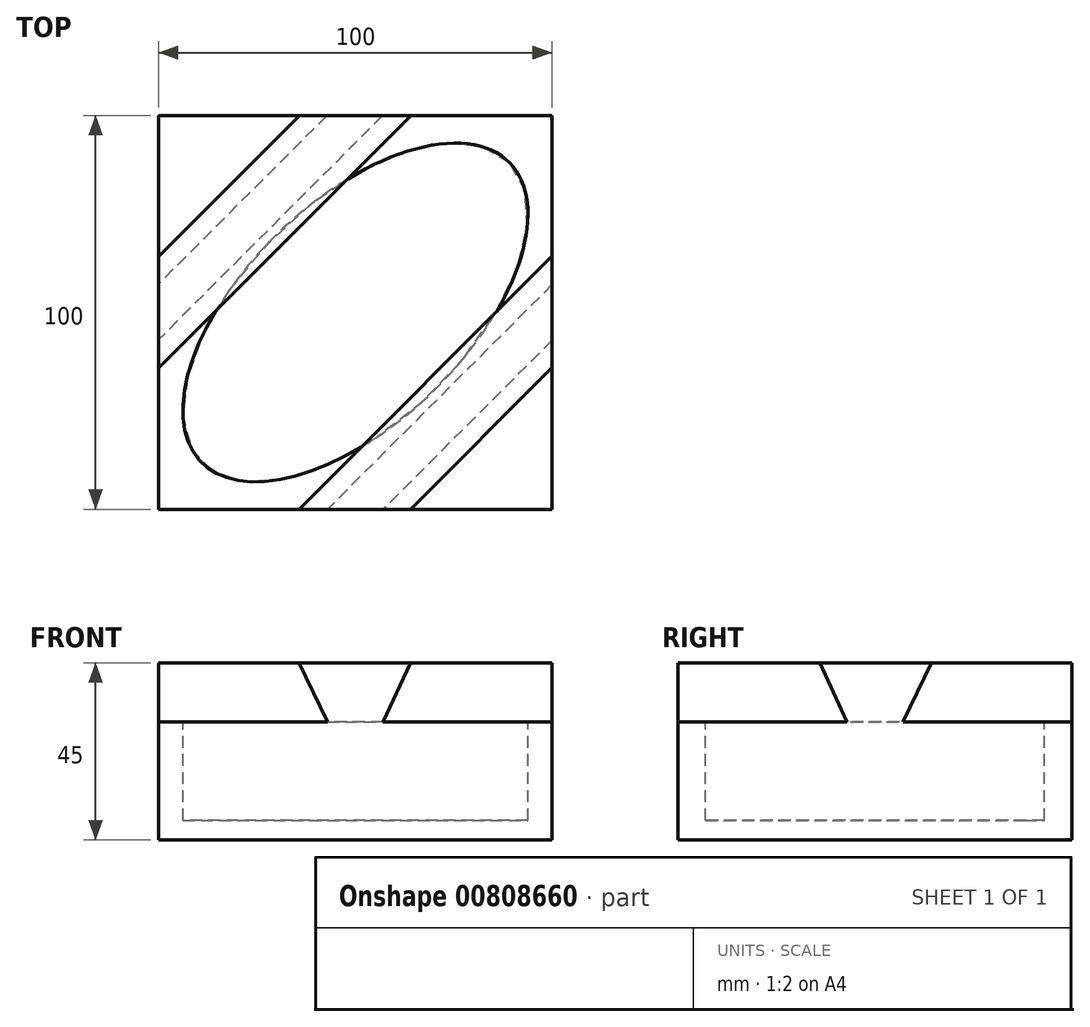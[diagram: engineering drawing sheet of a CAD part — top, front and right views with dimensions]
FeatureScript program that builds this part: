
annotation { "Feature Type Name" : "Feature", "Feature Type Description" : "" }
export const myFeature = defineFeature(function(context is Context, id is Id, definition is map)
    precondition{}
    {
        {
            var Q0;
            Q0=qCreatedBy(makeId("Top.planeOp"),FACE);
            var sketch = newSketch(context, id + "F0", { "sketchPlane" : qUnion([Q0])});
            skLineSegment(sketch, "E0.bottom", {"start": v(-50, 50) * mm, "end": v(50, 50) * mm});
            skLineSegment(sketch, "E0.top", {"start": v(-50, -50) * mm, "end": v(50, -50) * mm});
            skLineSegment(sketch, "E0.left", {"start": v(-50, 50) * mm, "end": v(-50, -50) * mm});
            skLineSegment(sketch, "E0.right", {"start": v(50, 50) * mm, "end": v(50, -50) * mm});
            skPoint(sketch, "E0.middle", {"position": v(0, 0) * mm});
            skLineSegment(sketch, "E1", {"start": v(50, -7.07) * mm, "end": v(7.07, -50) * mm});
            skLineSegment(sketch, "E2", {"start": v(46.46, 3.54) * mm, "end": v(50, 7.07) * mm});
            skLineSegment(sketch, "E3", {"start": v(46.46, 3.54) * mm, "end": v(-7.07, -50) * mm});
            skLineSegment(sketch, "E4", {"start": v(-50.16, 7.07) * mm, "end": v(-7.23, 50) * mm});
            skLineSegment(sketch, "E5", {"start": v(-46.62, -3.54) * mm, "end": v(-50.16, -7.07) * mm});
            skLineSegment(sketch, "E6", {"start": v(-46.62, -3.54) * mm, "end": v(6.91, 50) * mm});
            skSolve(sketch);
        }
        {
            var Q0;
            {var subQ0=sQuery(id+"F0.wireOp",EDGE,"E0.left");var subQ1=sQuery(id+"F0.wireOp",EDGE,"E0.bottom");var subQ2=makeQuery(id+"F0.imprint","INTERSECT",VERTEX,{"derivedFrom":[subQ1,subQ0]});Q0=makeQuery(id+"F0.imprint","IMPRINT",FACE,{"disambiguationData":[TD([[makeQuery(id+"F0.imprint","IMPRINT",EDGE,{"disambiguationData":[TD([[subQ2,-1.0]])],"derivedFrom":subQ1}),-1.0]])]});}
            var Q1;
            {var subQ3=sQuery(id+"F0.wireOp",EDGE,"E1");Q1=makeQuery(id+"F0.imprint","IMPRINT",FACE,{"disambiguationData":[TD([[makeQuery(id+"F0.imprint","IMPRINT",EDGE,{"derivedFrom":subQ3}),1.0]])]});}
            var Q2;
            {var subQ3=sQuery(id+"F0.wireOp",EDGE,"E2");Q2=makeQuery(id+"F0.imprint","IMPRINT",FACE,{"disambiguationData":[TD([[makeQuery(id+"F0.imprint","IMPRINT",EDGE,{"derivedFrom":subQ3}),1.0]])]});}
            var Q3;
            {var subQ7=sQuery(id+"F0.wireOp",EDGE,"E6");Q3=makeQuery(id+"F0.imprint","IMPRINT",FACE,{"disambiguationData":[TD([[makeQuery(id+"F0.imprint","IMPRINT",EDGE,{"derivedFrom":subQ7}),1.0]])]});}
            var Q4;
            {var subQ1=sQuery(id+"F0.wireOp",EDGE,"E1");Q4=makeQuery(id+"F0.imprint","IMPRINT",FACE,{"disambiguationData":[TD([[makeQuery(id+"F0.imprint","IMPRINT",EDGE,{"derivedFrom":subQ1}),-1.0]])]});}
            extrude(context, id + "F1", {"entities" : qUnion([Q0, Q1, Q2, Q3, Q4]), "depth" : 30 * mm, "offsetDistance" : 25 * mm});
        }
        {
            var Q0;
            Q0=makeQuery(id+"F1.opExtrude","CAP_FACE",FACE,{"disambiguationData":[OSD([sQuery(id+"F0.wireOp",EDGE,"E0.bottom"),sQuery(id+"F0.wireOp",EDGE,"E0.top"),sQuery(id+"F0.wireOp",EDGE,"E0.left"),sQuery(id+"F0.wireOp",EDGE,"E0.right")])],"isStart":false});
            cPlane(context, id + "F2", {"entities" : qUnion([Q0]), "cplaneType" : CPlaneType.OFFSET, "offset" : 0 * mm, "width" : 150 * mm, "height" : 150 * mm});
        }
        {
            var Q0;
            Q0=qCreatedBy(id+"F2.planeOp",FACE);
            var sketch = newSketch(context, id + "F3", { "sketchPlane" : qUnion([Q0])});
            skLineSegment(sketch, "E7.bottom", {"start": v(6.91, 50) * mm, "end": v(-7.23, 50) * mm});
            skLineSegment(sketch, "E7.top", {"start": v(7.07, -50) * mm, "end": v(-7.07, -50) * mm});
            skLineSegment(sketch, "E7.left", {"start": v(50, 7.07) * mm, "end": v(50, -7.07) * mm});
            skLineSegment(sketch, "E7.right", {"start": v(-50, 7.23) * mm, "end": v(-50, -6.91) * mm});
            skPoint(sketch, "E7.middle", {"position": v(0, 0) * mm});
            skLineSegment(sketch, "E8", {"start": v(-50, 0) * mm, "end": v(0, 50) * mm, "construction": true});
            skLineSegment(sketch, "E9", {"start": v(50, 0) * mm, "end": v(0, -50) * mm, "construction": true});
            skLineSegment(sketch, "E10.left", {"start": v(-7.23, 50) * mm, "end": v(-50, 7.23) * mm});
            skLineSegment(sketch, "E10.right", {"start": v(6.91, 50) * mm, "end": v(-50, -6.91) * mm});
            skLineSegment(sketch, "E11.left", {"start": v(50, 7.07) * mm, "end": v(-7.07, -50) * mm});
            skLineSegment(sketch, "E11.right", {"start": v(50, -7.07) * mm, "end": v(7.07, -50) * mm});
            skPoint(sketch, "E12.orphan", {"position": v(50, 50) * mm});
            skPoint(sketch, "E13.orphan", {"position": v(50, -50) * mm});
            skPoint(sketch, "E14.orphan", {"position": v(-50, -50) * mm});
            skPoint(sketch, "E15.orphan", {"position": v(-50, 50) * mm});
            skEllipse(sketch, "E16", {"center": v(0, 0) * mm, "majorRadius": 54.6 * mm, "minorRadius": 28.15 * mm, "majorAxis": v(0.72, 0.7)});
            skSolve(sketch);
        }
        {
            var Q0;
            Q0=qCreatedBy(id+"F2.planeOp",FACE);
            cPlane(context, id + "F4", {"entities" : qUnion([Q0]), "cplaneType" : CPlaneType.OFFSET, "offset" : 15 * mm, "width" : 150 * mm, "height" : 150 * mm});
        }
        {
            var Q0;
            Q0=qCreatedBy(id+"F4.planeOp",FACE);
            var sketch = newSketch(context, id + "F5", { "sketchPlane" : qUnion([Q0])});
            skLineSegment(sketch, "E17.left", {"start": v(-14.14, 50) * mm, "end": v(-50, 14.14) * mm});
            skLineSegment(sketch, "E17.right", {"start": v(14.14, 50) * mm, "end": v(-50, -14.14) * mm});
            skLineSegment(sketch, "E18.bottom", {"start": v(50, 50) * mm, "end": v(-50, 50) * mm, "construction": true});
            skLineSegment(sketch, "E18.top", {"start": v(50, -50) * mm, "end": v(-50, -50) * mm, "construction": true});
            skLineSegment(sketch, "E18.left", {"start": v(50, 50) * mm, "end": v(50, -50) * mm, "construction": true});
            skLineSegment(sketch, "E18.right", {"start": v(-50, 50) * mm, "end": v(-50, -50) * mm, "construction": true});
            skPoint(sketch, "E18.middle", {"position": v(0, 0) * mm});
            skLineSegment(sketch, "E19", {"start": v(0, 50) * mm, "end": v(-50, 0) * mm, "construction": true});
            skLineSegment(sketch, "E20", {"start": v(0, -50) * mm, "end": v(50, 0) * mm, "construction": true});
            skLineSegment(sketch, "E21", {"start": v(-25, 25) * mm, "end": v(-17.93, 17.93) * mm, "construction": true});
            skLineSegment(sketch, "E22", {"start": v(-25, 25) * mm, "end": v(-32.07, 32.07) * mm, "construction": true});
            skLineSegment(sketch, "E23", {"start": v(25, -25) * mm, "end": v(17.93, -17.93) * mm, "construction": true});
            skLineSegment(sketch, "E24", {"start": v(25, -25) * mm, "end": v(32.07, -32.07) * mm, "construction": true});
            skLineSegment(sketch, "E25.left", {"start": v(50, 14.34) * mm, "end": v(-14.34, -50) * mm});
            skLineSegment(sketch, "E25.right", {"start": v(50, -13.94) * mm, "end": v(13.94, -50) * mm});
            skLineSegment(sketch, "E26", {"start": v(-14.34, -50) * mm, "end": v(13.94, -50) * mm});
            skLineSegment(sketch, "E27", {"start": v(50, -13.94) * mm, "end": v(50, 14.34) * mm});
            skLineSegment(sketch, "E28", {"start": v(14.14, 50) * mm, "end": v(-14.14, 50) * mm});
            skLineSegment(sketch, "E29", {"start": v(-50, 14.14) * mm, "end": v(-50, -14.14) * mm});
            skSolve(sketch);
        }
        {
            var Q1;
            Q1=makeQuery(id+"F3.imprint","IMPRINT",FACE,{"disambiguationData":[TD([[makeQuery(id+"F3.imprint","IMPRINT",EDGE,{"derivedFrom":sQuery(id+"F3.wireOp",EDGE,"E7.bottom")}),1.0]])]});
            var Q2;
            Q2=makeQuery(id+"F5.imprint","IMPRINT",FACE,{"disambiguationData":[TD([[makeQuery(id+"F5.imprint","IMPRINT",EDGE,{"derivedFrom":sQuery(id+"F5.wireOp",EDGE,"E17.left")}),1.0]])]});
            loft(context, id + "F6", {"operationType" : NewBodyOperationType.ADD, "sheetProfilesArray" : [{ "sheetProfileEntities" : qUnion([Q1]) }, { "sheetProfileEntities" : qUnion([Q2]) }]});
        }
        {
            var Q1;
            Q1=makeQuery(id+"F3.imprint","IMPRINT",FACE,{"disambiguationData":[TD([[makeQuery(id+"F3.imprint","IMPRINT",EDGE,{"derivedFrom":sQuery(id+"F3.wireOp",EDGE,"E7.top")}),-1.0]])]});
            var Q2;
            Q2=makeQuery(id+"F5.imprint","IMPRINT",FACE,{"disambiguationData":[TD([[makeQuery(id+"F5.imprint","IMPRINT",EDGE,{"derivedFrom":sQuery(id+"F5.wireOp",EDGE,"E25.left")}),1.0]])]});
            loft(context, id + "F7", {"operationType" : NewBodyOperationType.ADD, "sheetProfilesArray" : [{ "sheetProfileEntities" : qUnion([Q1]) }, { "sheetProfileEntities" : qUnion([Q2]) }]});
        }
        {
            var Q0;
            Q0=makeQuery(id+"F3.imprint","IMPRINT",FACE,{"disambiguationData":[TD([[makeQuery(id+"F3.imprint","IMPRINT",EDGE,{"derivedFrom":sQuery(id+"F3.wireOp",EDGE,"E16")}),1.0]])]});
            extrude(context, id + "F8", {"entities" : qUnion([Q0]), "operationType" : NewBodyOperationType.REMOVE, "oppositeDirection" : true, "depth" : 25 * mm, "offsetDistance" : 25 * mm});
        }
    });
